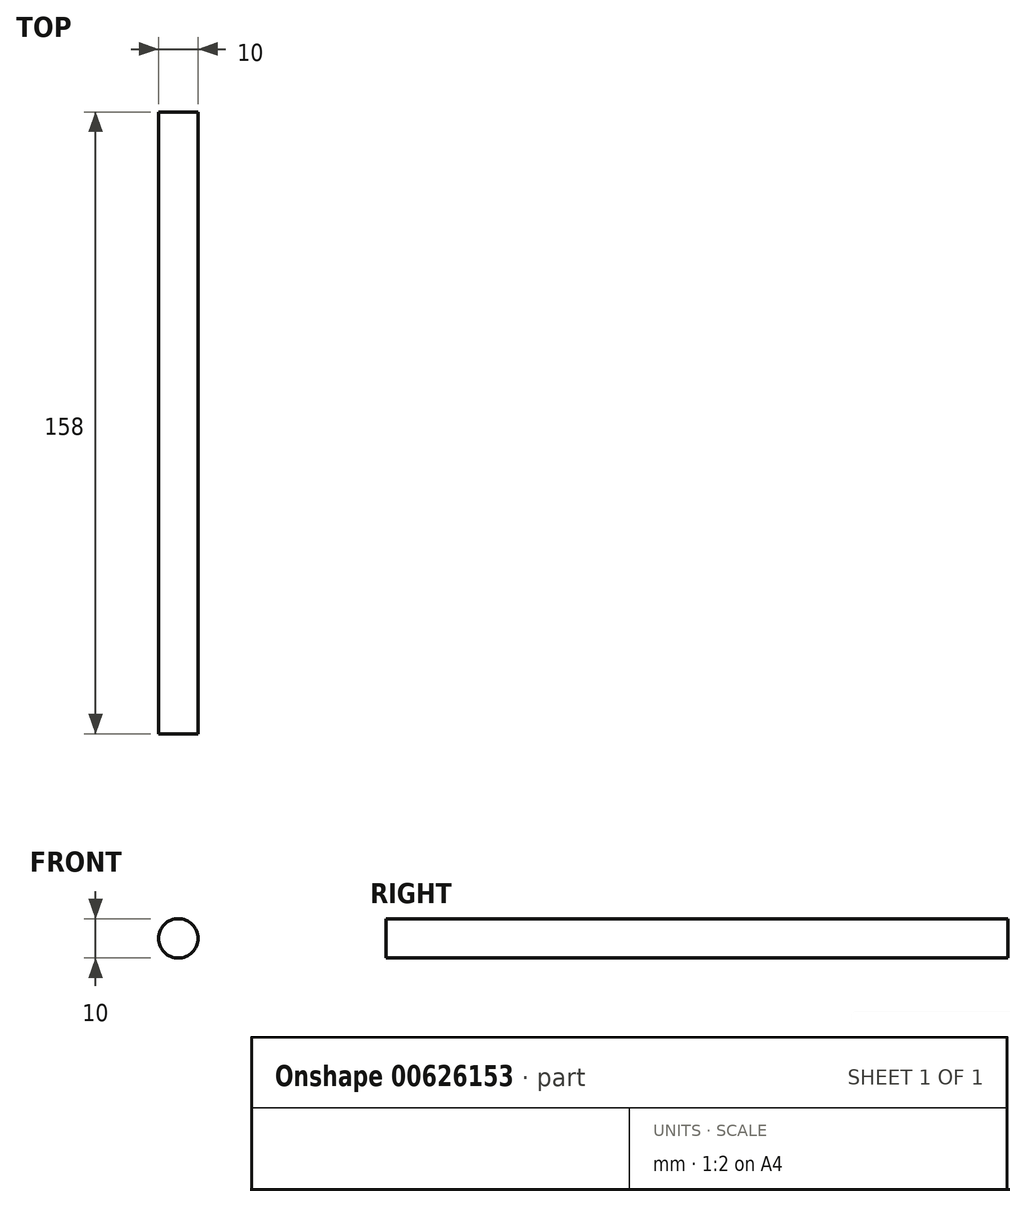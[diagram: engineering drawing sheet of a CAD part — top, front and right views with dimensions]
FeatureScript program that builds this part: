
annotation { "Feature Type Name" : "Feature", "Feature Type Description" : "" }
export const myFeature = defineFeature(function(context is Context, id is Id, definition is map)
    precondition{}
    {
        {
            var Q0;
            Q0=qCreatedBy(makeId("Front.planeOp"),FACE);
            var sketch = newSketch(context, id + "F0", { "sketchPlane" : qUnion([Q0])});
            skCircle(sketch, "E0", {"center": v(0, 0) * mm, "radius": 5 * mm});
            skSolve(sketch);
        }
        {
            var Q0;
            Q0=makeQuery(id+"F0.imprint","IMPRINT",FACE,{"disambiguationData":[TD([[makeQuery(id+"F0.imprint","IMPRINT",EDGE,{"derivedFrom":sQuery(id+"F0.wireOp",EDGE,"E0")}),1.0]])]});
            var Q1;
            Q1=sQuery(id+"F0.wireOp",EDGE,"E0");
            extrude(context, id + "F1", {"entities" : qUnion([Q0]), "surfaceEntities" : qUnion([Q1]), "depth" : 158 * mm, "offsetDistance" : 25 * mm});
        }
    });
